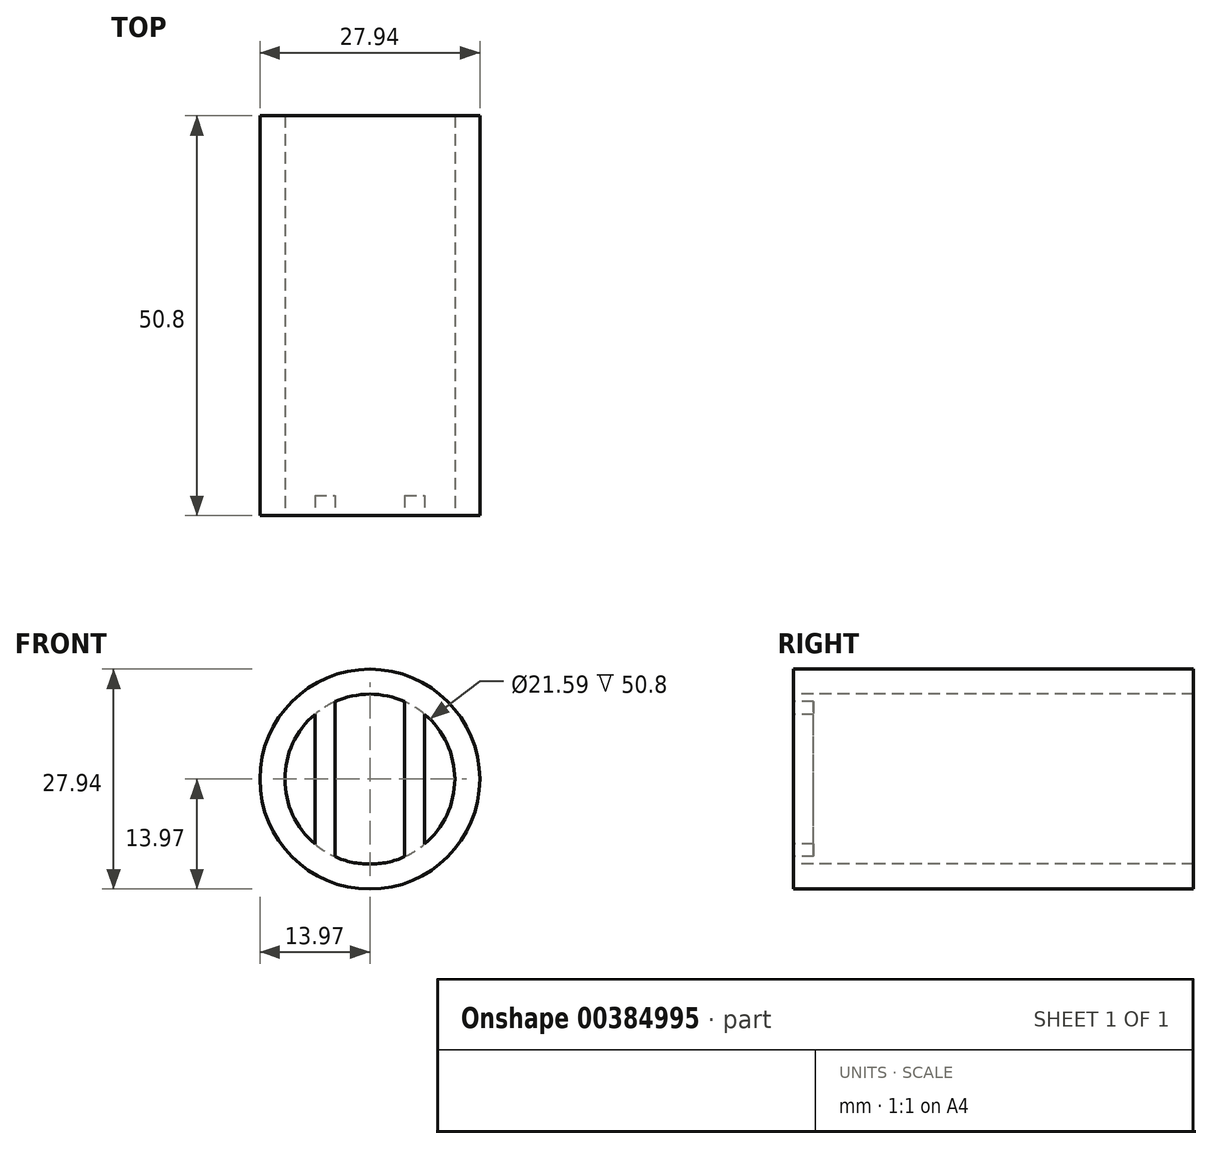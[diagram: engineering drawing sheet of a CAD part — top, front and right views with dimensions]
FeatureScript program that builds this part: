
annotation { "Feature Type Name" : "Feature", "Feature Type Description" : "" }
export const myFeature = defineFeature(function(context is Context, id is Id, definition is map)
    precondition{}
    {
        {
            var Q0;
            Q0=qCreatedBy(makeId("Front.planeOp"),FACE);
            var sketch = newSketch(context, id + "F0", { "sketchPlane" : qUnion([Q0])});
            skCircle(sketch, "E0", {"center": v(0, 0) * mm, "radius": 13.97 * mm});
            skSolve(sketch);
        }
        {
            var Q0;
            Q0 = qSketchRegion(id + "F0", true);
            extrude(context, id + "F1", {"entities" : qUnion([Q0]), "depth" : 50.8 * mm, "offsetDistance" : 25.4 * mm});
        }
        {
            var Q0;
            Q0=makeQuery(id+"F1.opExtrude","CAP_FACE",FACE,{"disambiguationData":[OSD([sQuery(id+"F0.wireOp",EDGE,"E0")])],"isStart":false});
            var sketch = newSketch(context, id + "F2", { "sketchPlane" : qUnion([Q0])});
            skCircle(sketch, "E1", {"center": v(0, 0) * mm, "radius": 10.8 * mm});
            skSolve(sketch);
        }
        {
            var Q0;
            Q0 = qSketchRegion(id + "F2", true);
            extrude(context, id + "F3", {"entities" : qUnion([Q0]), "operationType" : NewBodyOperationType.REMOVE, "oppositeDirection" : true, "depth" : 50.8 * mm, "offsetDistance" : 25.4 * mm});
        }
        {
            var Q0;
            Q0=makeQuery(id+"F1.opExtrude","CAP_FACE",FACE,{"disambiguationData":[OSD([sQuery(id+"F0.wireOp",EDGE,"E0")])],"isStart":false});
            var sketch = newSketch(context, id + "F4", { "sketchPlane" : qUnion([Q0])});
            skLineSegment(sketch, "E2", {"start": v(-4.43, -9.84) * mm, "end": v(-4.43, 9.84) * mm});
            skLineSegment(sketch, "E3", {"start": v(-4.43, -9.84) * mm, "end": v(-6.97, -9.84) * mm});
            skLineSegment(sketch, "E4", {"start": v(-6.97, -9.84) * mm, "end": v(-6.97, 9.82) * mm});
            skLineSegment(sketch, "E5", {"start": v(-6.97, 9.82) * mm, "end": v(-4.43, 9.84) * mm});
            skSolve(sketch);
        }
        {
            var Q0;
            {var subQ0=sQuery(id+"F4.wireOp",EDGE,"E2");Q0=makeQuery(id+"F4.imprint","IMPRINT",FACE,{"disambiguationData":[TD([[makeQuery(id+"F4.imprint","IMPRINT",EDGE,{"derivedFrom":subQ0}),1.0]])]});}
            extrude(context, id + "F5", {"entities" : qUnion([Q0]), "oppositeDirection" : true, "depth" : 2.54 * mm, "offsetDistance" : 25.4 * mm});
        }
        {
            var Q0;
            Q0=makeQuery(id+"F5.opExtrude","SWEPT_BODY",BODY,{"disambiguationData":[OSD([sQuery(id+"F2.wireOp",EDGE,"E1"),sQuery(id+"F4.wireOp",EDGE,"idPioBFV-gpLu-Oc1Y-5w7k-Wq62l72PzdcQ"),sQuery(id+"F4.wireOp",EDGE,"E2")])]});
            var Q1;
            Q1=qCreatedBy(makeId("Right.planeOp"),FACE);
            mirror(context, id + "F6", {"operationType" : NewBodyOperationType.ADD, "entities" : qUnion([Q0]), "mirrorPlane" : qUnion([Q1])});
        }
    });
